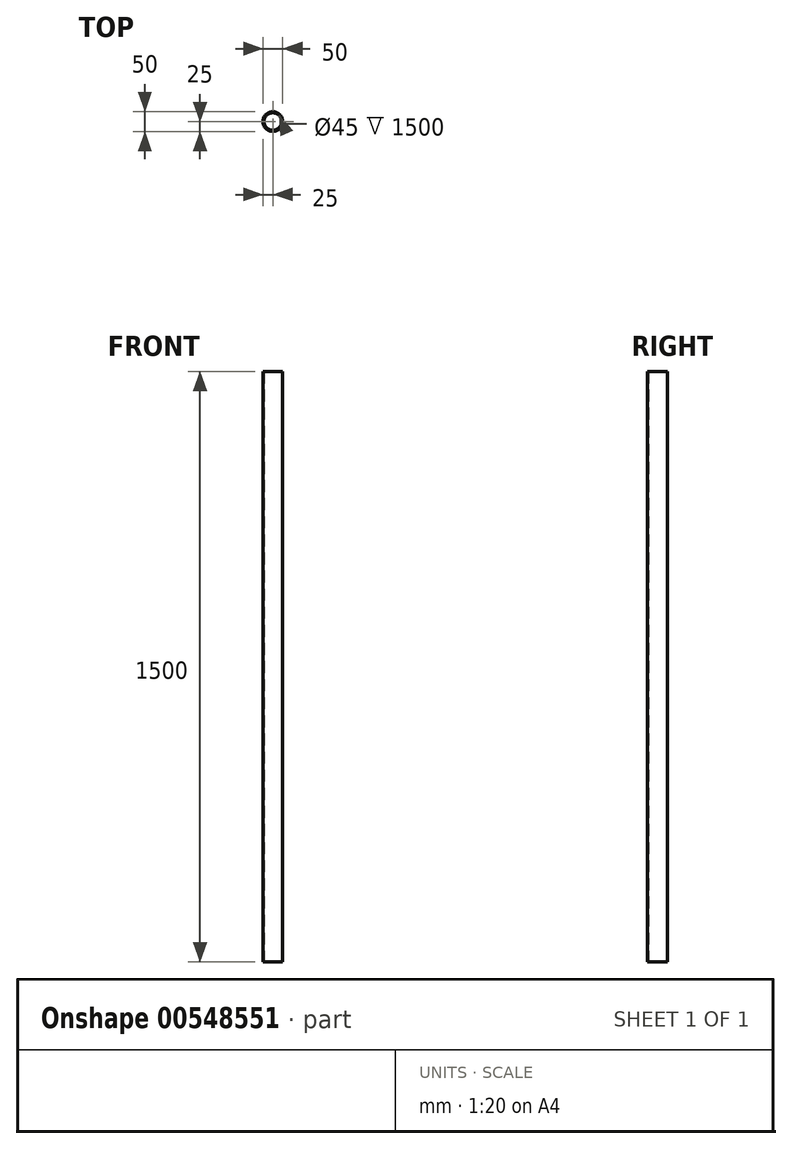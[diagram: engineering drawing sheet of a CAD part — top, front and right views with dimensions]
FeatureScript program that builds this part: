
annotation { "Feature Type Name" : "Feature", "Feature Type Description" : "" }
export const myFeature = defineFeature(function(context is Context, id is Id, definition is map)
    precondition{}
    {
        {
            var Q0;
            Q0=qCreatedBy(makeId("Top.planeOp"),FACE);
            var sketch = newSketch(context, id + "F0", { "sketchPlane" : qUnion([Q0])});
            skCircle(sketch, "E0", {"center": v(0, 0) * mm, "radius": 22.5 * mm});
            skCircle(sketch, "E1", {"center": v(0, 0) * mm, "radius": 25 * mm});
            skSolve(sketch);
        }
        {
            var Q0;
            Q0 = qSketchRegion(id + "F0", true);
            extrude(context, id + "F1", {"entities" : qUnion([Q0]), "depth" : 1500 * mm, "offsetDistance" : 25 * mm});
        }
    });
